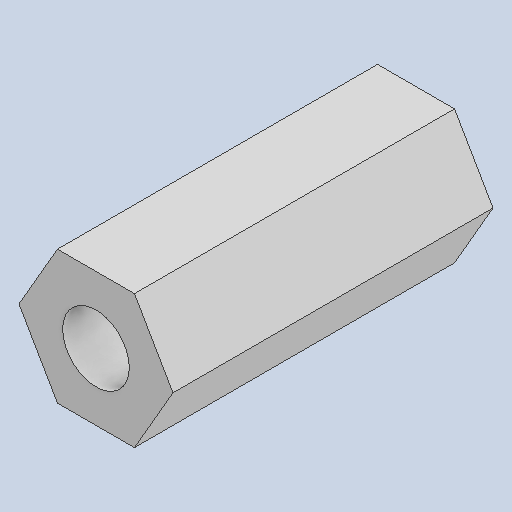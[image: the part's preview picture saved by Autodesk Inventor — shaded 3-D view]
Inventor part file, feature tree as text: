
AUTODESK INVENTOR PART (.ipt)
format: ipt  version: 2024.2 (Build 282272000, 272)  size: 98,816 bytes
history: native  units: mm
features: extrude x2, sketch x1
ambient origin geometry x8: Origin, YZ Plane, XZ Plane, XY Plane, X Axis, Y Axis, Z Axis, Center Point
bodies: Solid1 (feature_tree)
feature tree (3):
  extrude  "Extrusion1"  Depth=12.0mm TaperAngle=0.0deg
  extrude  "Extrusion3"  Depth=12.0mm
  sketch  "Sketch1"  dims[d0=5.0mm d1=12.0mm d2=0.0mm d6=2.5mm d7=7.0mm d8=0.0mm]
